# Revit family: HC_Manifold_MEPcontent_Henco_Underfloor Manifold UFH-MDK_4CH_INT-EN
name_source: partatom
category: Mechanical Equipment
units: mm (PartAtom-declared; Revit-internal decimal feet)

## family parameters
Always vertical = Yes
Cut with Voids When Loaded = No
Maintain Annotation Orientation = No
OmniClass Number = 23.75.70.00
OmniClass Title = HVAC Distribution Devices
Part Type = Normal
Room Calculation Point = No
Round Connector Dimension = Use Diameter
Shared = No
Work Plane-Based = No

## types (1)
- 4CH
    Article Description = 4-GROUP UNDERFLOOR MANIFOLD UFH-MDK
    Article Type = 4CH
    Base Family Version = 24.06
    Black = Color RGB 029-029-029
    Centre distance between secondary connections = 50 mm
    Connection Caps = Color RGB 212-171-033
    Content Supplier URL = www.MEPcontent.com
    Custom = No
    Default Elevation = 0 mm  [stored 0 ft]
    Description = 4-GROUP UNDERFLOOR MANIFOLD UFH-MDK
    Drain Connection = Color RGB 199-194-189
    EMCS Version = 4.0
    ETIM Article Class = EC010382
    Family Version = 11.27
    GLN = 5414764000001
    GTIN = 5414764341685
    IFCExportAs = IFCValve
    L1+M1 = 28 mm
    L17 = 290 mm  [stored 0.951444 ft]
    L5 = 43 mm
    MEPcontent Class = DISTRIBUTOR_HC
    Main Body = Color RGB 029-029-029
    Manufacturer = Henco
    Manufacturer Art. No. = UFH-0605MDK4
    Manufacturer URL = www.henco.be
    Max. percentage of glycol = 40%
    Max. test pressure with cold water = 10 bars
    Max. working pressure = 6 bars
    Model = 4CH
    Number of Arrays = 4
    Number of Groups = 4
    Primary Connection Diameter = 25.4 mm  [stored 0.0833333 ft]
    Primary connections (CH) = 1"
    Product Line = Henco
    Revit Version = 2022
    Secondary Connection Diameter = 19 mm  [stored 0.062336 ft]
    Secondary connections (UFH) = 3/4"
    Thermometer scale = 0°C - 60°C
    Thermostatic Valve = Color RGB 255-255-255
    URL = https://mep.trimble.com
    Use Nominal Diameter = Yes

note: [stored X ft] marks values corroborated as IEEE doubles in the binary element streams (Revit-internal decimal feet)

## geometry (parser evidence)
native form markers: Sweep x12
no freeform markers — native parametric forms only
